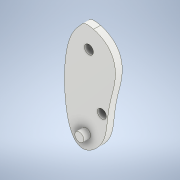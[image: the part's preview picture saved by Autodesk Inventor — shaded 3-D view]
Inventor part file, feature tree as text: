
AUTODESK INVENTOR PART (.ipt)
format: ipt  version: 2022 (Build 260153000, 153)  size: 137,728 bytes
history: native  units: in
note: dims shown in document units (in); Inventor stores cm internally (conversion verified against a paired STEP export)
features: extrude x3, sketch x2, projected_geometry x1
ambient origin geometry x8: Origin, YZ Plane, XZ Plane, XY Plane, X Axis, Y Axis, Z Axis, Center Point
bodies: Solid1 (feature_tree)
feature tree (6):
  sketch  "Sketch2"  dims[d0=0.1969in d1=0.0in d2=0.1969in d3=0.0in]
  extrude  "Extrusion1"  Depth=0.1969in TaperAngle=0.0deg
  extrude  "Extrusion2"  Depth=0.2559in
  extrude  "Extrusion3"  [1 undecoded]
  sketch  "Sketch3"  dims[d4=0.1969in d5=0.0in d8=0.2559in]
  projected_geometry  "Projected Loop2"
note: 1 required parameter value undecoded (feature->parameter linkage not recoverable at this tier; creation-order binding heuristic only, values carry confidence <= 0.55)
